# Revit family: SANINDUSA_140022004_Urb.y_Urb.y65WDclosecoupledtoilet365x650x400_V0
name_source: partatom
category: Plumbing Fixtures
revit_build: Autodesk Revit 2018 (Build: 20170223_1515(x64)
units: mm (PartAtom-declared; Revit-internal decimal feet)

## family parameters
Cut with Voids When Loaded = No
Host = Face
Part Type = Normal
Room Calculation Point = No
Round Connector Dimension = Use Diameter
Shared = No

## types (1)
- SANINDUSA_140022004_Urb.y_Urb.y65WDclosecoupledtoilet365x650x400_V0
    AssetType = Fixed
    CodePerformance = EN 997:2012  CL 1 - 6 A
    Color = white
    Constituents = Compatible toilet seats (not included): 2403100-Toilet seat urb.y clipoff with slow close system; 2401100-Toilet seat urb.y clipoff. Compatible cisterns (not included): 140111004LM - 65 Urb.y bottom water supply connection cistern with dual flush mechanism; 140113004LM - 65 Urb.y side water supply connection cistern with dual flush mechanism. 24-fixing kit (included)
    Default Elevation = 1219 mm
    Description = Soil appliance for the disposal of excrement.
    DrainSize = 100 mm  [stored 0.328084 ft]
    Element Type = TOILETPAN: Soil appliance for the disposal of excrement.
    Features = "Domestic and commercial use. Versatile timeless design. Seats with clipoff system easy to clean and slow close option. Back to wall WC. "
    Finish = gloss
    InletDiameter = 0 mm  [stored 0 ft]
    Installation Instructions = https://www.tec.sanindusa.pt
    InstallationDate = 1900-12-31T23:59:59
    Manufacturer = Sanindusa
    ManufacturerName = Sanindusa
    ManufacturerURL = www.tec.sanindusa.pt
    Material = vitreous china
    Model = 140022004
    ModelNumber = 140022004
    ModelReference = Urb.y
    Name = Urb.y 65 W|D close coupled toilet
    NominalHeight = 400 mm  [stored 1.31234 ft]
    NominalLength = 365 mm  [stored 1.19751 ft]
    NominalWidth = 365 mm  [stored 1.19751 ft]
    PanColor = white
    PanMaterial = vitreous china
    PanMounting = pedestal
    Pre-defined type (IFC) = TOILETPAN
    ProductInformation = https://www.tec.sanindusa.pt
    ProductionYear = 2015
    Size = 365x650x400
    ToiletPanType = washdown
    ToiletType = LooseCoupled
    Type (IFC) = IfcSanitaryTerminalType
    URL = www.tec.sanindusa.pt
    Uniclass2015Code = Pr_40_20_93_94
    Uniclass2015Title = WC pans
    Uniclass2015Version = Products v1.6
    Version = 1
    WarrantyDescription = https://www.tec.sanindusa.pt
    WarrantyDurationParts = 5
    WarrantyDurationUnit = year
    WarrantyStartDate = 1900-12-31T23:59:59
    Waste Connection = Yes
    Weight = 31.00 kg

note: [stored X ft] marks values corroborated as IEEE doubles in the binary element streams (Revit-internal decimal feet)

## geometry (parser evidence)
native form markers: Sweep x7
no freeform markers — native parametric forms only
